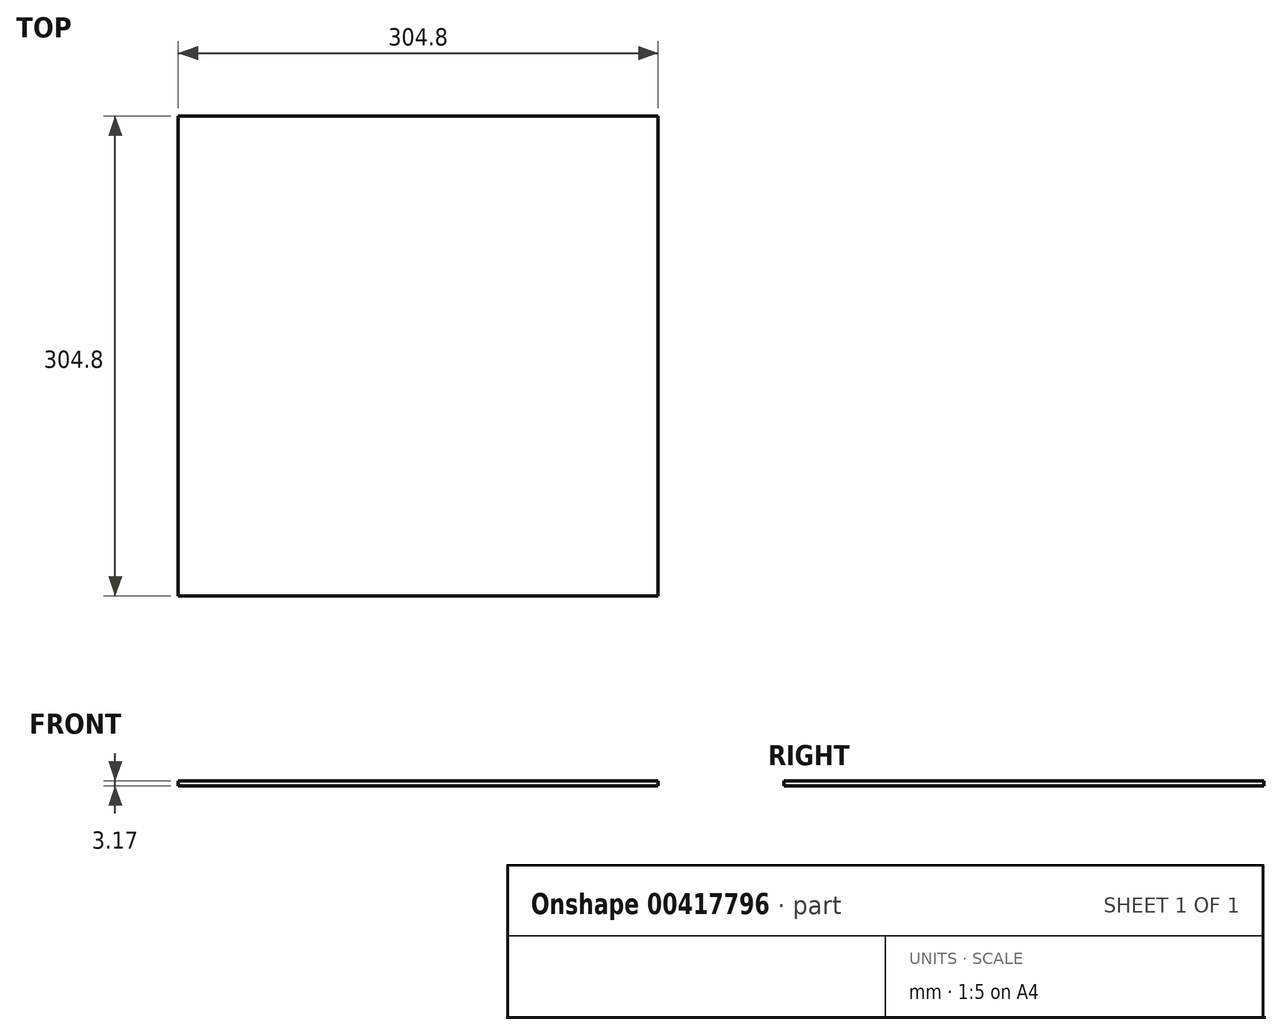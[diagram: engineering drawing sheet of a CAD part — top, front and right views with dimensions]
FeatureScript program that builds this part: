
annotation { "Feature Type Name" : "Feature", "Feature Type Description" : "" }
export const myFeature = defineFeature(function(context is Context, id is Id, definition is map)
    precondition{}
    {
        {
            var Q0;
            Q0=qCreatedBy(makeId("Top.planeOp"),FACE);
            var sketch = newSketch(context, id + "F0", { "sketchPlane" : qUnion([Q0])});
            skLineSegment(sketch, "E0.bottom", {"start": v(-149.99, -115.45) * mm, "end": v(154.81, -115.45) * mm});
            skLineSegment(sketch, "E0.top", {"start": v(-149.99, 189.35) * mm, "end": v(154.81, 189.35) * mm});
            skLineSegment(sketch, "E0.left", {"start": v(-149.99, -115.45) * mm, "end": v(-149.99, 189.35) * mm});
            skLineSegment(sketch, "E0.right", {"start": v(154.81, -115.45) * mm, "end": v(154.81, 189.35) * mm});
            skSolve(sketch);
        }
        {
            var Q0;
            Q0=makeQuery(id+"F0.imprint","IMPRINT",FACE,{"disambiguationData":[TD([[makeQuery(id+"F0.imprint","IMPRINT",EDGE,{"derivedFrom":sQuery(id+"F0.wireOp",EDGE,"E0.bottom")}),1.0]])]});
            extrude(context, id + "F1", {"entities" : qUnion([Q0]), "depth" : 3.17 * mm});
        }
    });
